# Revit family: Krowne_14-802L_WallMount_Faucet
name_source: partatom
category: Plumbing Fixtures
revit_build: Autodesk Revit 2018 (Build: 20190510_1515(x64)
units: mm (PartAtom-declared; Revit-internal decimal feet)

## family parameters
Always vertical = Yes
Cut with Voids When Loaded = No
OmniClass Number = 23.40.40.00
OmniClass Title = Food Service Equipment and Furnishings
Part Type = Normal
Room Calculation Point = No
Round Connector Dimension = Use Diameter
Shared = No
Work Plane-Based = No

## types (1)
- DefaultType
    Assembly Code = E1090300
    Cold Water Connection Height = 0"
    Cold Water Flow = 2 GPM
    Cold Water Maximum Pressure = 0.00 psi
    Cold Water Minimum Pressure = 0.00 psi
    Cold Water Size = 1"
    Cold Water Temperature Recommended = -460 °F
    Depth = 1 7/8"
    Description = Wall Mount Faucet
    Foodservice Equipment Identifier = Yes
    Height = 3 15/16"
    Hot Water Connection Height = 0"
    Hot Water Consumption = 0 GPM
    Hot Water Flow = 2 GPM
    Hot Water Maximum Pressure = 0.00 psi
    Hot Water Minimum Pressure = 0.00 psi
    Hot Water Size = 1"
    Hot Water Temperature = 100 °F
    KCL SpecSheet URL = http://kclweb.kclcad.com
    KCLRef = KCL2C9,,0004c576-0000-0000-0000-000000000307,KR,14-802L ,637099800680000000,c64d4556-9eae-4a66-8f8a-d065013fd965,1413a27f-e5d5-4681-b70d-183254c7a9d2
    Manufacturer = Krowne Metal
    Model = 14-802L
    URL = https://krowne.com
    Weight in Pounds = 5
    Width = 12"

## geometry (parser evidence)
native form markers: Sweep x4
no freeform markers — native parametric forms only
